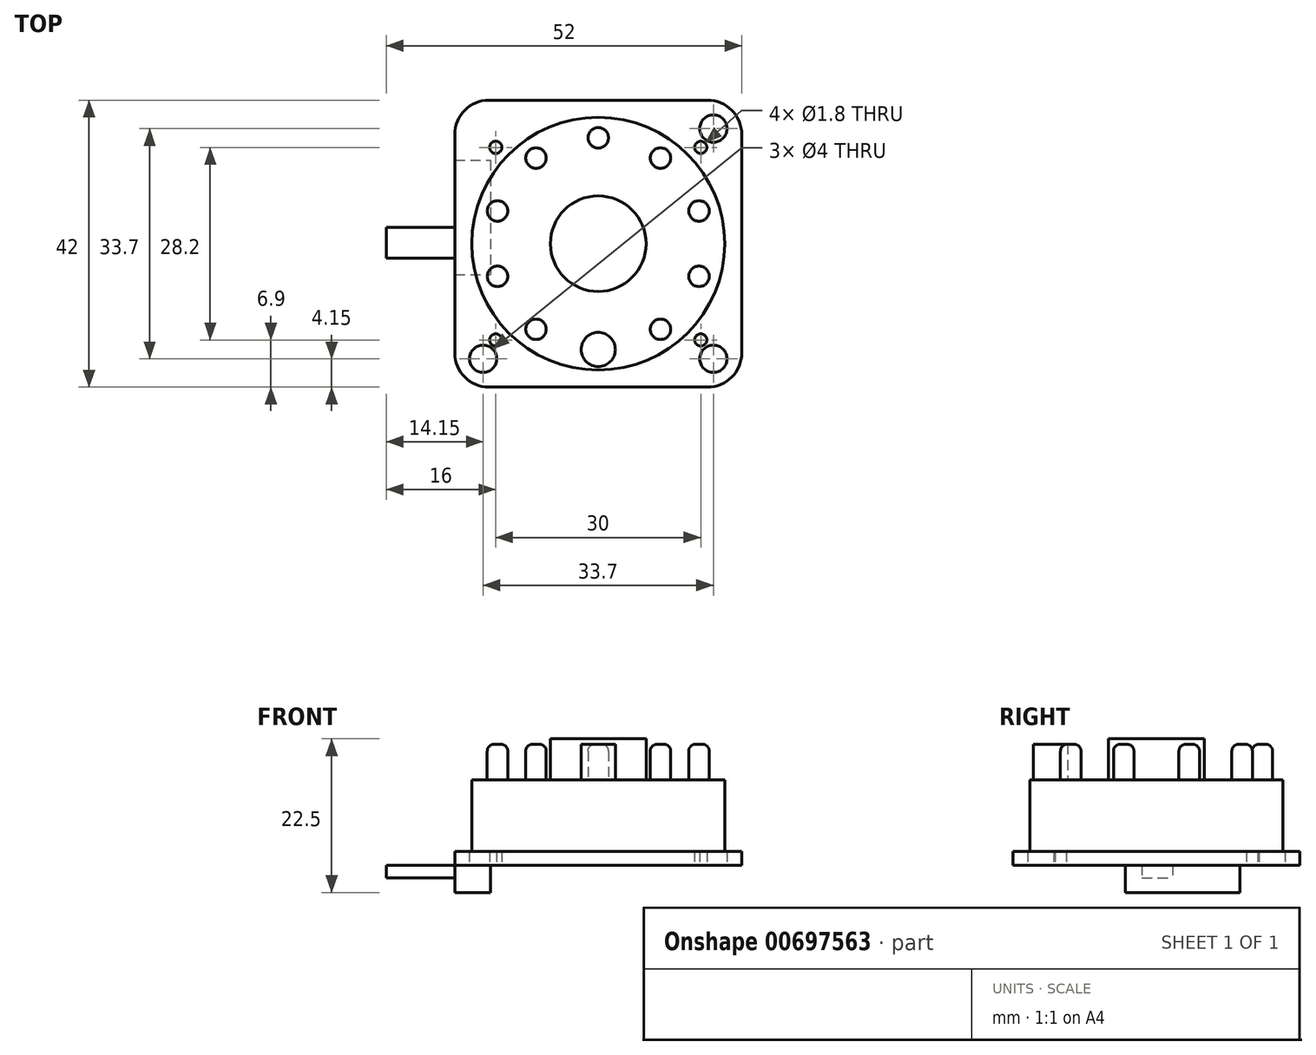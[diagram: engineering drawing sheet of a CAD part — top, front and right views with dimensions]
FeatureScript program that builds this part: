
annotation { "Feature Type Name" : "Feature", "Feature Type Description" : "" }
export const myFeature = defineFeature(function(context is Context, id is Id, definition is map)
    precondition{}
    {
        {
            var Q0;
            Q0=qCreatedBy(makeId("Top.planeOp"),FACE);
            var sketch = newSketch(context, id + "F0", { "sketchPlane" : qUnion([Q0])});
            skLineSegment(sketch, "E0.bottom", {"start": v(21, -21) * mm, "end": v(-21, -21) * mm});
            skLineSegment(sketch, "E0.top", {"start": v(21, 21) * mm, "end": v(-21, 21) * mm});
            skLineSegment(sketch, "E0.left", {"start": v(21, -21) * mm, "end": v(21, 21) * mm});
            skLineSegment(sketch, "E0.right", {"start": v(-21, -21) * mm, "end": v(-21, 21) * mm});
            skPoint(sketch, "E0.middle", {"position": v(0, 0) * mm});
            skCircle(sketch, "E1", {"center": v(-16.85, 16.85) * mm, "radius": 2 * mm});
            skCircle(sketch, "E2.MirrorC", {"center": v(16.85, 16.85) * mm, "radius": 2 * mm});
            skCircle(sketch, "E3", {"center": v(15, 14.1) * mm, "radius": 0.9 * mm});
            skCircle(sketch, "E4.MirrorC", {"center": v(-15, 14.1) * mm, "radius": 0.9 * mm});
            skCircle(sketch, "E5.MirrorC", {"center": v(-15, -14.1) * mm, "radius": 0.9 * mm});
            skCircle(sketch, "E6.MirrorC", {"center": v(15, -14.1) * mm, "radius": 0.9 * mm});
            skCircle(sketch, "E7.MirrorC", {"center": v(16.85, -16.85) * mm, "radius": 2 * mm});
            skCircle(sketch, "E8.MirrorC", {"center": v(-16.85, -16.85) * mm, "radius": 2 * mm});
            skSolve(sketch);
        }
        {
            var Q0;
            Q0 = qSketchRegion(id + "F0", true);
            var Q1;
            Q1=makeQuery(id+"F0.imprint","IMPRINT",FACE,{"disambiguationData":[TD([[makeQuery(id+"F0.imprint","IMPRINT",EDGE,{"derivedFrom":sQuery(id+"F0.wireOp",EDGE,"E2.MirrorC")}),-1.0]])]});
            var Q2;
            Q2=makeQuery(id+"F0.imprint","IMPRINT",FACE,{"disambiguationData":[TD([[makeQuery(id+"F0.imprint","IMPRINT",EDGE,{"derivedFrom":sQuery(id+"F0.wireOp",EDGE,"E1")}),1.0]])]});
            extrude(context, id + "F1", {"entities" : qUnion([Q0, Q1, Q2]), "depth" : 2 * mm, "offsetDistance" : 25 * mm});
        }
        {
            var Q0;
            Q0=makeQuery(id+"F1.opExtrude","SWEPT_EDGE",EDGE,{"disambiguationData":[OSD([sQuery(id+"F0.wireOp",EDGE,"E0.top"),sQuery(id+"F0.wireOp",EDGE,"E0.left")])]});
            var Q1;
            Q1=makeQuery(id+"F1.opExtrude","SWEPT_EDGE",EDGE,{"disambiguationData":[OSD([sQuery(id+"F0.wireOp",EDGE,"E0.top"),sQuery(id+"F0.wireOp",EDGE,"E0.right")])]});
            var Q2;
            Q2=makeQuery(id+"F1.opExtrude","SWEPT_EDGE",EDGE,{"disambiguationData":[OSD([sQuery(id+"F0.wireOp",EDGE,"E0.bottom"),sQuery(id+"F0.wireOp",EDGE,"E0.right")])]});
            var Q3;
            Q3=makeQuery(id+"F1.opExtrude","SWEPT_EDGE",EDGE,{"disambiguationData":[OSD([sQuery(id+"F0.wireOp",EDGE,"E0.bottom"),sQuery(id+"F0.wireOp",EDGE,"E0.left")])]});
            fillet(context, id + "F2", {"entities" : qUnion([Q0, Q1, Q2, Q3]), "tangentPropagation" : true, "radius" : 5 * mm, "defaultsChanged" : false, "vertexSettings" : [], "allowEdgeOverflow" : false});
        }
        {
            var Q0;
            Q0=makeQuery(id+"F1.opExtrude","CAP_FACE",FACE,{"disambiguationData":[OSD([sQuery(id+"F0.wireOp",EDGE,"E0.bottom"),sQuery(id+"F0.wireOp",EDGE,"E0.top"),sQuery(id+"F0.wireOp",EDGE,"E0.left"),sQuery(id+"F0.wireOp",EDGE,"E0.right"),sQuery(id+"F0.wireOp",EDGE,"E1"),sQuery(id+"F0.wireOp",EDGE,"E2.MirrorC"),sQuery(id+"F0.wireOp",EDGE,"E3"),sQuery(id+"F0.wireOp",EDGE,"E4.MirrorC"),sQuery(id+"F0.wireOp",EDGE,"E5.MirrorC"),sQuery(id+"F0.wireOp",EDGE,"E6.MirrorC")])],"isStart":false});
            var sketch = newSketch(context, id + "F3", { "sketchPlane" : qUnion([Q0])});
            skCircle(sketch, "E9", {"center": v(0, 0) * mm, "radius": 18.5 * mm});
            skSolve(sketch);
        }
        {
            var Q0;
            Q0 = qSketchRegion(id + "F3", true);
            extrude(context, id + "F4", {"entities" : qUnion([Q0]), "operationType" : NewBodyOperationType.ADD, "depth" : 10.5 * mm, "offsetDistance" : 25 * mm});
        }
        {
            var Q0;
            Q0=makeQuery(id+"F4.opExtrude","CAP_FACE",FACE,{"disambiguationData":[OSD([sQuery(id+"F3.wireOp",EDGE,"E9")])],"isStart":false});
            var sketch = newSketch(context, id + "F5", { "sketchPlane" : qUnion([Q0])});
            skCircle(sketch, "E10", {"center": v(0, 0) * mm, "radius": 7 * mm});
            skSolve(sketch);
        }
        {
            var Q0;
            Q0 = qSketchRegion(id + "F5", true);
            extrude(context, id + "F6", {"entities" : qUnion([Q0]), "operationType" : NewBodyOperationType.ADD, "depth" : 6 * mm, "offsetDistance" : 25 * mm});
        }
        {
            var Q0;
            Q0=makeQuery(id+"F4.opExtrude","CAP_FACE",FACE,{"disambiguationData":[OSD([sQuery(id+"F3.wireOp",EDGE,"E9")])],"isStart":false});
            var sketch = newSketch(context, id + "F7", { "sketchPlane" : qUnion([Q0])});
            skCircle(sketch, "E11", {"center": v(0, -15.5) * mm, "radius": 2.5 * mm});
            skCircle(sketch, "E12", {"center": v(0, -15.5) * mm, "radius": 1.5 * mm});
            skCircle(sketch, "E13.1.0", {"center": v(9.11, -12.54) * mm, "radius": 1.5 * mm});
            skCircle(sketch, "E13.2.0", {"center": v(14.74, -4.79) * mm, "radius": 1.5 * mm});
            skCircle(sketch, "E13.3.0", {"center": v(14.74, 4.79) * mm, "radius": 1.5 * mm});
            skCircle(sketch, "E13.4.0", {"center": v(9.11, 12.54) * mm, "radius": 1.5 * mm});
            skCircle(sketch, "E13.5.0", {"center": v(0, 15.5) * mm, "radius": 1.5 * mm});
            skCircle(sketch, "E13.6.0", {"center": v(-9.11, 12.54) * mm, "radius": 1.5 * mm});
            skCircle(sketch, "E13.7.0", {"center": v(-14.74, 4.79) * mm, "radius": 1.5 * mm});
            skCircle(sketch, "E13.8.0", {"center": v(-14.74, -4.79) * mm, "radius": 1.5 * mm});
            skCircle(sketch, "E13.9.0", {"center": v(-9.11, -12.54) * mm, "radius": 1.5 * mm});
            skPoint(sketch, "E13.center", {"position": v(0, 0) * mm});
            skSolve(sketch);
        }
        {
            var Q0;
            Q0 = qSketchRegion(id + "F7", true);
            var Q1;
            Q1=makeQuery(id+"F7.imprint","IMPRINT",FACE,{"disambiguationData":[TD([[makeQuery(id+"F7.imprint","IMPRINT",EDGE,{"derivedFrom":sQuery(id+"F7.wireOp",EDGE,"E12")}),1.0]])]});
            extrude(context, id + "F8", {"entities" : qUnion([Q0, Q1]), "operationType" : NewBodyOperationType.ADD, "depth" : 5.2 * mm, "offsetDistance" : 25 * mm});
        }
        {
            var Q0;
            Q0=makeQuery(id+"F8.opExtrude","CAP_EDGE",EDGE,{"disambiguationData":[OSD([sQuery(id+"F7.wireOp",EDGE,"E13.2.0")])],"isStart":false});
            var Q1;
            Q1=makeQuery(id+"F8.opExtrude","CAP_FACE",FACE,{"disambiguationData":[OSD([sQuery(id+"F7.wireOp",EDGE,"E13.3.0")])],"isStart":false});
            var Q2;
            Q2=makeQuery(id+"F8.opExtrude","CAP_FACE",FACE,{"disambiguationData":[OSD([sQuery(id+"F7.wireOp",EDGE,"E13.1.0")])],"isStart":false});
            var Q3;
            Q3=makeQuery(id+"F8.opExtrude","CAP_FACE",FACE,{"disambiguationData":[OSD([sQuery(id+"F7.wireOp",EDGE,"E13.9.0")])],"isStart":false});
            var Q4;
            Q4=makeQuery(id+"F8.opExtrude","CAP_FACE",FACE,{"disambiguationData":[OSD([sQuery(id+"F7.wireOp",EDGE,"E13.8.0")])],"isStart":false});
            var Q5;
            Q5=makeQuery(id+"F8.opExtrude","CAP_FACE",FACE,{"disambiguationData":[OSD([sQuery(id+"F7.wireOp",EDGE,"E13.7.0")])],"isStart":false});
            var Q6;
            Q6=makeQuery(id+"F8.opExtrude","CAP_FACE",FACE,{"disambiguationData":[OSD([sQuery(id+"F7.wireOp",EDGE,"E13.6.0")])],"isStart":false});
            var Q7;
            Q7=makeQuery(id+"F8.opExtrude","CAP_FACE",FACE,{"disambiguationData":[OSD([sQuery(id+"F7.wireOp",EDGE,"E13.5.0")])],"isStart":false});
            var Q8;
            Q8=makeQuery(id+"F8.opExtrude","CAP_FACE",FACE,{"disambiguationData":[OSD([sQuery(id+"F7.wireOp",EDGE,"E13.4.0")])],"isStart":false});
            fillet(context, id + "F9", {"entities" : qUnion([Q0, Q1, Q2, Q3, Q4, Q5, Q6, Q7, Q8]), "tangentPropagation" : true, "radius" : 1 * mm, "defaultsChanged" : false, "vertexSettings" : [], "allowEdgeOverflow" : false});
        }
        {
            var Q0;
            Q0=makeQuery(id+"F1.opExtrude","CAP_FACE",FACE,{"disambiguationData":[OSD([sQuery(id+"F0.wireOp",EDGE,"E0.bottom"),sQuery(id+"F0.wireOp",EDGE,"E0.top"),sQuery(id+"F0.wireOp",EDGE,"E0.left"),sQuery(id+"F0.wireOp",EDGE,"E0.right"),sQuery(id+"F0.wireOp",EDGE,"E1"),sQuery(id+"F0.wireOp",EDGE,"E2.MirrorC"),sQuery(id+"F0.wireOp",EDGE,"E3"),sQuery(id+"F0.wireOp",EDGE,"E4.MirrorC"),sQuery(id+"F0.wireOp",EDGE,"E5.MirrorC"),sQuery(id+"F0.wireOp",EDGE,"E6.MirrorC")])],"isStart":true});
            var sketch = newSketch(context, id + "F10", { "sketchPlane" : qUnion([Q0])});
            skLineSegment(sketch, "E14.bottom", {"start": v(-21, -12.2) * mm, "end": v(-15.76, -12.2) * mm});
            skLineSegment(sketch, "E14.top", {"start": v(-21, 4.52) * mm, "end": v(-15.76, 4.52) * mm});
            skLineSegment(sketch, "E14.left", {"start": v(-21, -12.2) * mm, "end": v(-21, 4.52) * mm});
            skLineSegment(sketch, "E14.right", {"start": v(-15.76, -12.2) * mm, "end": v(-15.76, 4.52) * mm});
            skSolve(sketch);
        }
        {
            var Q0;
            Q0 = qSketchRegion(id + "F10", true);
            extrude(context, id + "F11", {"entities" : qUnion([Q0]), "operationType" : NewBodyOperationType.ADD, "depth" : 4 * mm, "offsetDistance" : 25 * mm});
        }
        {
            var Q0;
            Q0=makeQuery(id+"F11.boolean.opBoolean","MERGE",FACE,{"derivedFrom":[makeQuery(id+"F1.opExtrude","SWEPT_FACE",FACE,{"disambiguationData":[OSD([sQuery(id+"F0.wireOp",EDGE,"E0.right")])]}),makeQuery(id+"F11.opExtrude","SWEPT_FACE",FACE,{"disambiguationData":[OSD([sQuery(id+"F10.wireOp",EDGE,"E14.left")])]})]});
            var sketch = newSketch(context, id + "F12", { "sketchPlane" : qUnion([Q0])});
            skLineSegment(sketch, "E15.bottom", {"start": v(2.12, 0) * mm, "end": v(-2.4, 0) * mm});
            skLineSegment(sketch, "E15.top", {"start": v(2.12, -1.9) * mm, "end": v(-2.4, -1.9) * mm});
            skLineSegment(sketch, "E15.left", {"start": v(2.12, 0) * mm, "end": v(2.12, -1.9) * mm});
            skLineSegment(sketch, "E15.right", {"start": v(-2.4, 0) * mm, "end": v(-2.4, -1.9) * mm});
            skSolve(sketch);
        }
        {
            var Q0;
            Q0 = qSketchRegion(id + "F12", true);
            extrude(context, id + "F13", {"entities" : qUnion([Q0]), "operationType" : NewBodyOperationType.ADD, "depth" : 10 * mm, "offsetDistance" : 25 * mm});
        }
    });
